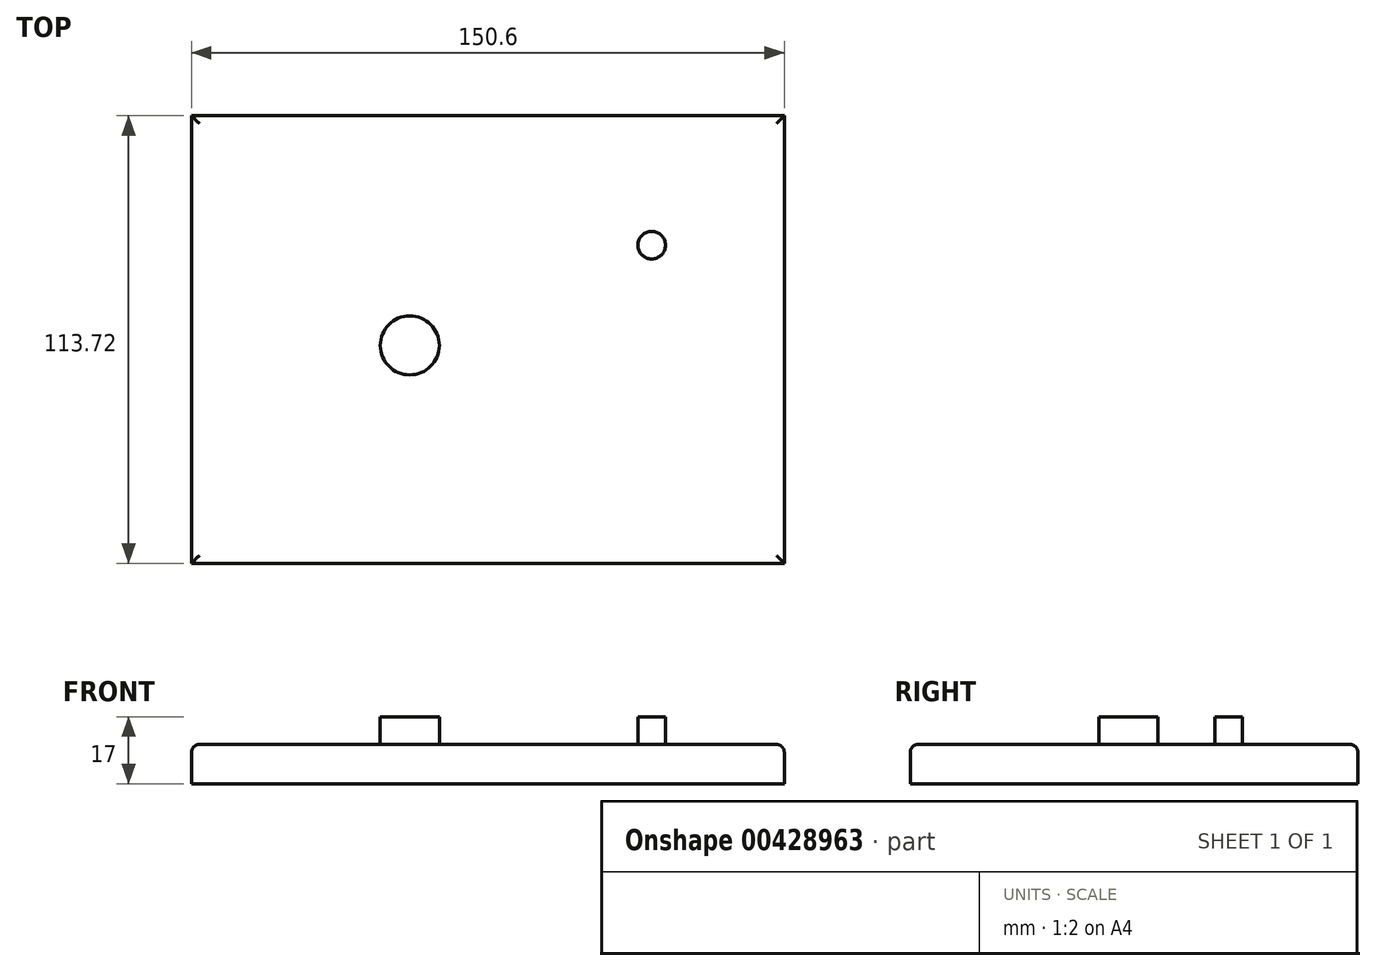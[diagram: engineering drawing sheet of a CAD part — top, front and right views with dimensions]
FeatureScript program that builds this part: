
annotation { "Feature Type Name" : "Feature", "Feature Type Description" : "" }
export const myFeature = defineFeature(function(context is Context, id is Id, definition is map)
    precondition{}
    {
        {
            var Q0;
            Q0=qCreatedBy(makeId("Top.planeOp"),FACE);
            var sketch = newSketch(context, id + "F0", { "sketchPlane" : qUnion([Q0])});
            skLineSegment(sketch, "E0.bottom", {"start": v(-75.3, 56.86) * mm, "end": v(75.3, 56.86) * mm});
            skLineSegment(sketch, "E0.top", {"start": v(-75.3, -56.86) * mm, "end": v(75.3, -56.86) * mm});
            skLineSegment(sketch, "E0.left", {"start": v(-75.3, 56.86) * mm, "end": v(-75.3, -56.86) * mm});
            skLineSegment(sketch, "E0.right", {"start": v(75.3, 56.86) * mm, "end": v(75.3, -56.86) * mm});
            skPoint(sketch, "E0.middle", {"position": v(0, 0) * mm});
            skLineSegment(sketch, "E1", {"start": v(-75.3, -1.48) * mm, "end": v(16.42, -1.48) * mm, "construction": true});
            skLineSegment(sketch, "E2", {"start": v(-19.85, -56.86) * mm, "end": v(-19.85, 14.85) * mm, "construction": true});
            skPoint(sketch, "E3", {"position": v(-19.85, -1.48) * mm});
            skCircle(sketch, "E4", {"center": v(-19.85, -1.48) * mm, "radius": 50 * mm, "construction": true});
            skCircle(sketch, "E5", {"center": v(-19.85, -1.48) * mm, "radius": 7.5 * mm});
            skLineSegment(sketch, "E6", {"start": v(75.3, 23.98) * mm, "end": v(41.6, 23.98) * mm, "construction": true});
            skLineSegment(sketch, "E7", {"start": v(41.6, 23.98) * mm, "end": v(41.6, 56.86) * mm, "construction": true});
            skCircle(sketch, "E8", {"center": v(41.6, 23.98) * mm, "radius": 3.5 * mm});
            skSolve(sketch);
        }
        {
            var Q0;
            Q0=makeQuery(id+"F0.imprint","IMPRINT",FACE,{"disambiguationData":[TD([[makeQuery(id+"F0.imprint","IMPRINT",EDGE,{"derivedFrom":sQuery(id+"F0.wireOp",EDGE,"E0.bottom")}),-1.0]])]});
            var Q1;
            Q1=makeQuery(id+"F0.imprint","IMPRINT",FACE,{"disambiguationData":[TD([[makeQuery(id+"F0.imprint","IMPRINT",EDGE,{"derivedFrom":sQuery(id+"F0.wireOp",EDGE,"E5")}),1.0]])]});
            var Q2;
            Q2=makeQuery(id+"F0.imprint","IMPRINT",FACE,{"disambiguationData":[TD([[makeQuery(id+"F0.imprint","IMPRINT",EDGE,{"derivedFrom":sQuery(id+"F0.wireOp",EDGE,"E8")}),1.0]])]});
            extrude(context, id + "F1", {"entities" : qUnion([Q0, Q1, Q2]), "depth" : 10 * mm});
        }
        {
            var Q0;
            Q0=makeQuery(id+"F1.opExtrude","CAP_EDGE",EDGE,{"disambiguationData":[OSD([sQuery(id+"F0.wireOp",EDGE,"E0.top")])],"isStart":false});
            var Q1;
            Q1=makeQuery(id+"F1.opExtrude","CAP_EDGE",EDGE,{"disambiguationData":[OSD([sQuery(id+"F0.wireOp",EDGE,"E0.left")])],"isStart":false});
            var Q2;
            Q2=makeQuery(id+"F1.opExtrude","CAP_EDGE",EDGE,{"disambiguationData":[OSD([sQuery(id+"F0.wireOp",EDGE,"E0.bottom")])],"isStart":false});
            var Q3;
            Q3=makeQuery(id+"F1.opExtrude","CAP_EDGE",EDGE,{"disambiguationData":[OSD([sQuery(id+"F0.wireOp",EDGE,"E0.right")])],"isStart":false});
            fillet(context, id + "F2", {"entities" : qUnion([Q0, Q1, Q2, Q3]), "radius" : 2 * mm, "tangentPropagation" : true, "allowEdgeOverflow" : false});
        }
        {
            var Q0;
            Q0=makeQuery(id+"F0.imprint","IMPRINT",FACE,{"disambiguationData":[TD([[makeQuery(id+"F0.imprint","IMPRINT",EDGE,{"derivedFrom":sQuery(id+"F0.wireOp",EDGE,"E5")}),1.0]])]});
            var Q1;
            Q1=makeQuery(id+"F0.imprint","IMPRINT",FACE,{"disambiguationData":[TD([[makeQuery(id+"F0.imprint","IMPRINT",EDGE,{"derivedFrom":sQuery(id+"F0.wireOp",EDGE,"E8")}),1.0]])]});
            extrude(context, id + "F3", {"entities" : qUnion([Q0, Q1]), "operationType" : NewBodyOperationType.ADD, "depth" : 17 * mm});
        }
    });
